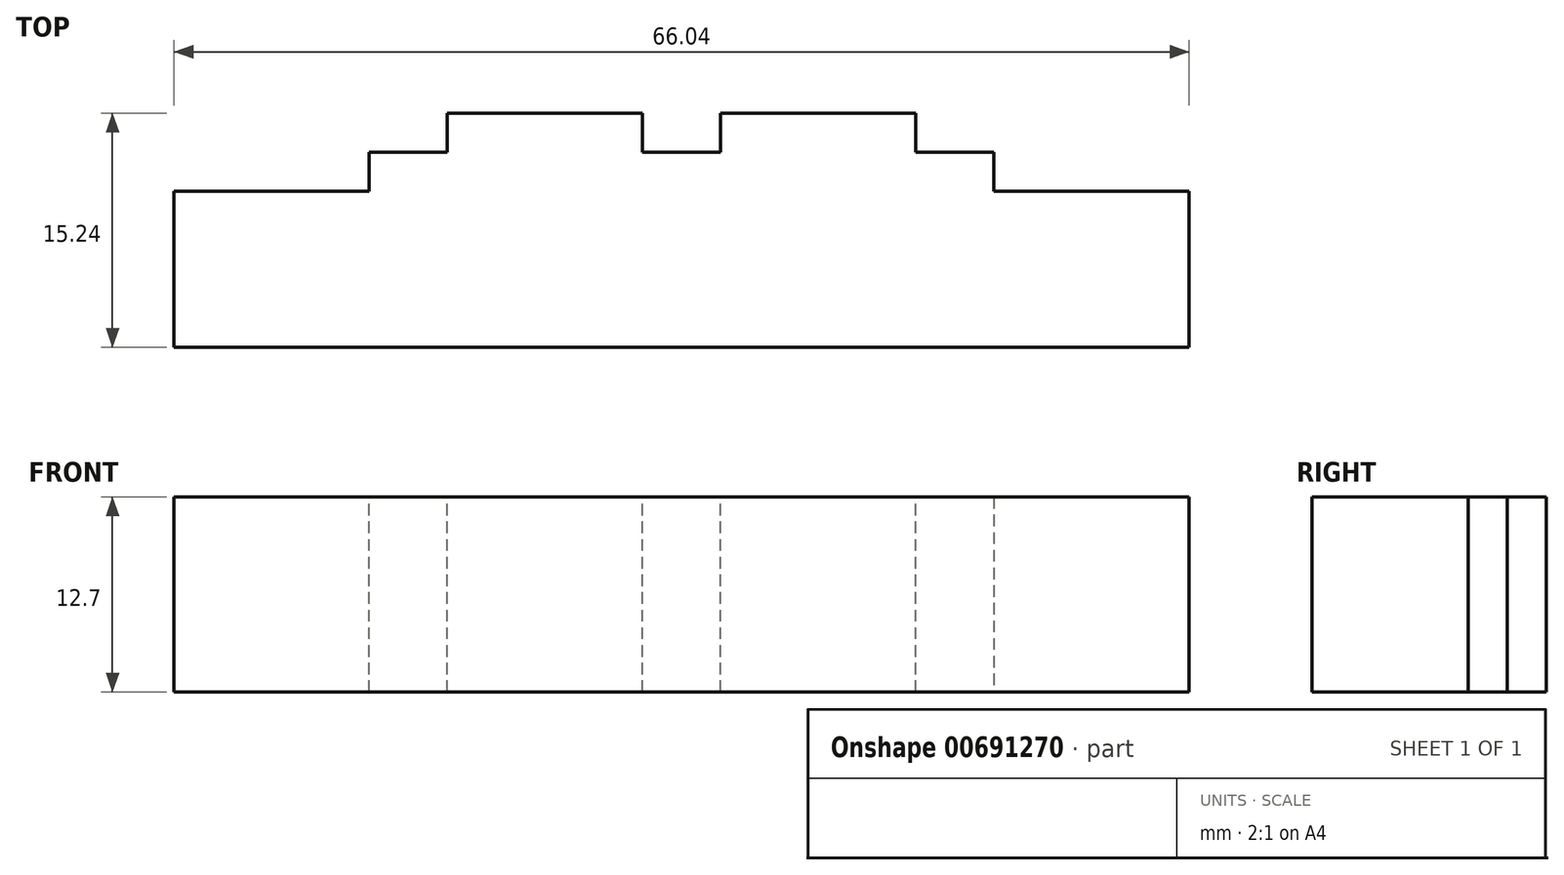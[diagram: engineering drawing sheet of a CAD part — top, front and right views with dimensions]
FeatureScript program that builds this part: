
annotation { "Feature Type Name" : "Feature", "Feature Type Description" : "" }
export const myFeature = defineFeature(function(context is Context, id is Id, definition is map)
    precondition{}
    {
        {
            var Q0;
            Q0=qCreatedBy(makeId("Top.planeOp"),FACE);
            var sketch = newSketch(context, id + "F0", { "sketchPlane" : qUnion([Q0])});
            skLineSegment(sketch, "E0", {"start": v(0, 0) * mm, "end": v(66.04, 0) * mm});
            skLineSegment(sketch, "E1", {"start": v(0, 0) * mm, "end": v(0, -10.16) * mm});
            skLineSegment(sketch, "E2", {"start": v(66.04, 0) * mm, "end": v(66.04, -10.16) * mm});
            skLineSegment(sketch, "E3", {"start": v(0, -10.16) * mm, "end": v(66.04, -10.16) * mm});
            skSolve(sketch);
        }
        {
            var Q0;
            Q0=makeQuery(id+"F0.imprint","IMPRINT",FACE,{"disambiguationData":[TD([[makeQuery(id+"F0.imprint","IMPRINT",EDGE,{"derivedFrom":sQuery(id+"F0.wireOp",EDGE,"E0")}),-1.0]])]});
            extrude(context, id + "F1", {"entities" : qUnion([Q0]), "depth" : 12.7 * mm, "offsetDistance" : 25.4 * mm});
        }
        {
            var Q0;
            Q0=makeQuery(id+"F1.opExtrude","SWEPT_FACE",FACE,{"disambiguationData":[OSD([sQuery(id+"F0.wireOp",EDGE,"E0")])]});
            var sketch = newSketch(context, id + "F2", { "sketchPlane" : qUnion([Q0])});
            skLineSegment(sketch, "E4", {"start": v(-66.04, 0) * mm, "end": v(-66.04, 12.7) * mm});
            skLineSegment(sketch, "E5", {"start": v(-66.04, 12.7) * mm, "end": v(0, 12.7) * mm});
            skLineSegment(sketch, "E6", {"start": v(0, 12.7) * mm, "end": v(0, 0) * mm});
            skLineSegment(sketch, "E7", {"start": v(0, 0) * mm, "end": v(-12.7, 0) * mm});
            skLineSegment(sketch, "E8", {"start": v(-12.7, 0) * mm, "end": v(-17.78, 0) * mm});
            skLineSegment(sketch, "E9", {"start": v(-17.78, 0) * mm, "end": v(-30.48, 0) * mm});
            skLineSegment(sketch, "E10", {"start": v(-30.48, 0) * mm, "end": v(-35.56, 0) * mm});
            skLineSegment(sketch, "E11", {"start": v(-35.56, 0) * mm, "end": v(-48.26, 0) * mm});
            skLineSegment(sketch, "E12", {"start": v(-48.26, 0) * mm, "end": v(-53.34, 0) * mm});
            skLineSegment(sketch, "E13", {"start": v(-53.34, 0) * mm, "end": v(-66.04, 0) * mm});
            skLineSegment(sketch, "E14", {"start": v(-53.34, 12.7) * mm, "end": v(-53.34, 0) * mm});
            skLineSegment(sketch, "E15", {"start": v(-48.26, 0) * mm, "end": v(-48.26, 12.7) * mm});
            skLineSegment(sketch, "E16", {"start": v(-30.48, 0) * mm, "end": v(-30.48, 12.7) * mm});
            skLineSegment(sketch, "E17", {"start": v(-35.56, 0) * mm, "end": v(-35.56, 12.7) * mm});
            skLineSegment(sketch, "E18", {"start": v(-17.78, 0) * mm, "end": v(-17.78, 12.7) * mm});
            skLineSegment(sketch, "E19", {"start": v(-12.7, 0) * mm, "end": v(-12.7, 12.7) * mm});
            skSolve(sketch);
        }
        {
            var Q0;
            Q0=makeQuery(id+"F2.imprint","IMPRINT",FACE,{"disambiguationData":[TD([[makeQuery(id+"F2.imprint","IMPRINT",EDGE,{"derivedFrom":sQuery(id+"F2.wireOp",EDGE,"E9")}),-1.0]])]});
            var Q1;
            Q1=makeQuery(id+"F2.imprint","IMPRINT",FACE,{"disambiguationData":[TD([[makeQuery(id+"F2.imprint","IMPRINT",EDGE,{"derivedFrom":sQuery(id+"F2.wireOp",EDGE,"E11")}),-1.0]])]});
            extrude(context, id + "F3", {"entities" : qUnion([Q0, Q1]), "operationType" : NewBodyOperationType.ADD, "depth" : 5.08 * mm, "offsetDistance" : 25.4 * mm});
        }
        {
            var Q0;
            Q0=makeQuery(id+"F2.imprint","IMPRINT",FACE,{"disambiguationData":[TD([[makeQuery(id+"F2.imprint","IMPRINT",EDGE,{"derivedFrom":sQuery(id+"F2.wireOp",EDGE,"E8")}),-1.0]])]});
            var Q1;
            Q1=makeQuery(id+"F2.imprint","IMPRINT",FACE,{"disambiguationData":[TD([[makeQuery(id+"F2.imprint","IMPRINT",EDGE,{"derivedFrom":sQuery(id+"F2.wireOp",EDGE,"E10")}),-1.0]])]});
            var Q2;
            Q2=makeQuery(id+"F2.imprint","IMPRINT",FACE,{"disambiguationData":[TD([[makeQuery(id+"F2.imprint","IMPRINT",EDGE,{"derivedFrom":sQuery(id+"F2.wireOp",EDGE,"E12")}),-1.0]])]});
            extrude(context, id + "F4", {"entities" : qUnion([Q0, Q1, Q2]), "operationType" : NewBodyOperationType.ADD, "depth" : 2.54 * mm, "offsetDistance" : 25.4 * mm});
        }
    });
